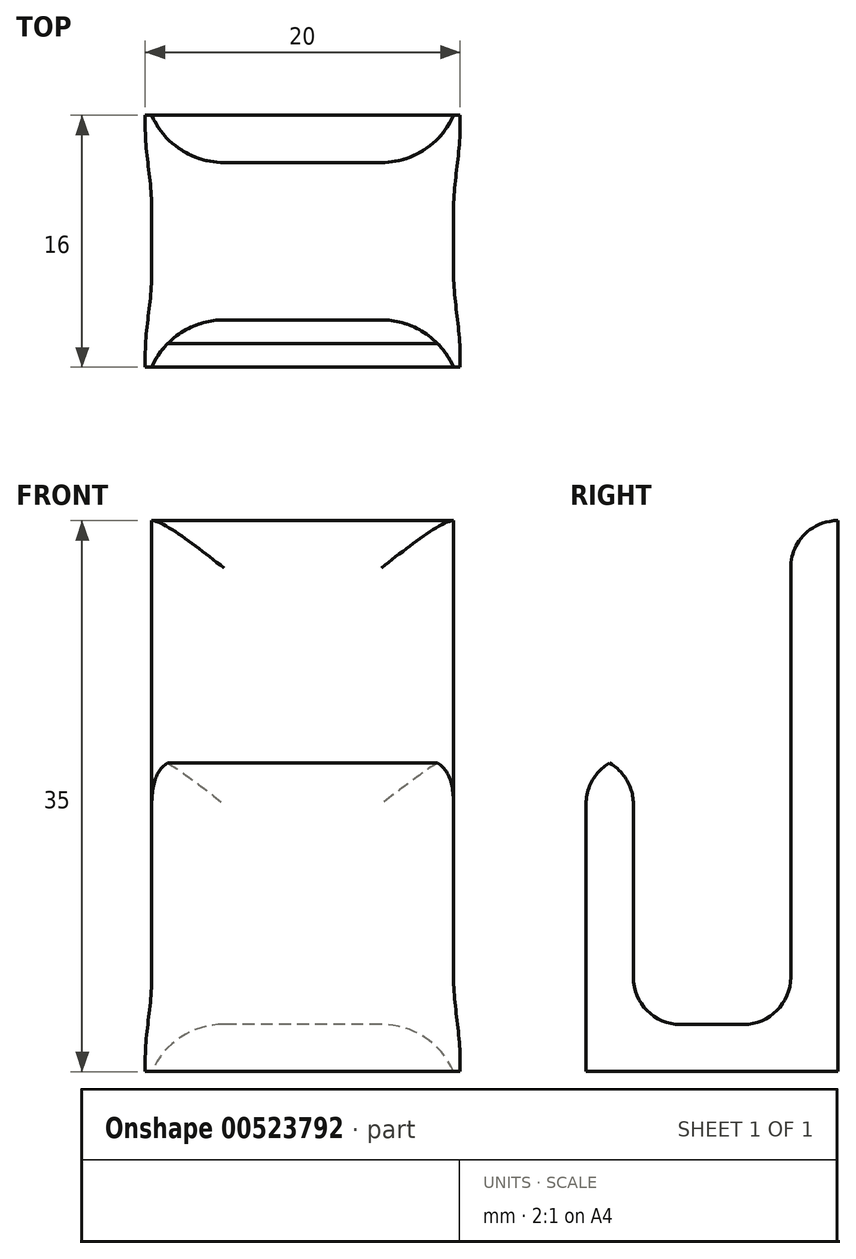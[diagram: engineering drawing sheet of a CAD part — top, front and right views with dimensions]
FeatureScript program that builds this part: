
annotation { "Feature Type Name" : "Feature", "Feature Type Description" : "" }
export const myFeature = defineFeature(function(context is Context, id is Id, definition is map)
    precondition{}
    {
        {
            var Q0;
            Q0=qCreatedBy(makeId("Right.planeOp"),FACE);
            var sketch = newSketch(context, id + "F0", { "sketchPlane" : qUnion([Q0])});
            skLineSegment(sketch, "E0.bottom", {"start": v(0, 24.94) * mm, "end": v(-3, 24.94) * mm});
            skLineSegment(sketch, "E0.left", {"start": v(0, 24.94) * mm, "end": v(0, -10.06) * mm});
            skLineSegment(sketch, "E0.right", {"start": v(-3, 24.94) * mm, "end": v(-3, -7.06) * mm});
            skLineSegment(sketch, "E1.top", {"start": v(-3, -7.06) * mm, "end": v(-13, -7.06) * mm});
            skLineSegment(sketch, "E2.top", {"start": v(-13, 9.94) * mm, "end": v(-16, 9.94) * mm});
            skLineSegment(sketch, "E2.left", {"start": v(-13, -7.06) * mm, "end": v(-13, 9.94) * mm});
            skLineSegment(sketch, "E2.right", {"start": v(-16, -10.06) * mm, "end": v(-16, 9.94) * mm});
            skLineSegment(sketch, "E3", {"start": v(0, -10.06) * mm, "end": v(-16, -10.06) * mm});
            skSolve(sketch);
        }
        {
            var Q0;
            Q0=makeQuery(id+"F0.imprint","IMPRINT",FACE,{"disambiguationData":[TD([[makeQuery(id+"F0.imprint","IMPRINT",EDGE,{"derivedFrom":sQuery(id+"F0.wireOp",EDGE,"E0.bottom")}),1.0]])]});
            extrude(context, id + "F1", {"entities" : qUnion([Q0]), "depth" : 20 * mm, "offsetDistance" : 25 * mm});
        }
        {
            var Q0;
            Q0=makeQuery(id+"F1.opExtrude","SWEPT_EDGE",EDGE,{"disambiguationData":[OSD([sQuery(id+"F0.wireOp",EDGE,"E0.bottom"),sQuery(id+"F0.wireOp",EDGE,"E0.right")])]});
            var Q1;
            Q1=makeQuery(id+"F1.opExtrude","SWEPT_EDGE",EDGE,{"disambiguationData":[OSD([sQuery(id+"F0.wireOp",EDGE,"E1.top"),sQuery(id+"F0.wireOp",EDGE,"E2.left")])]});
            var Q2;
            Q2=makeQuery(id+"F1.opExtrude","SWEPT_EDGE",EDGE,{"disambiguationData":[OSD([sQuery(id+"F0.wireOp",EDGE,"E2.top"),sQuery(id+"F0.wireOp",EDGE,"E2.left")])]});
            var Q3;
            Q3=makeQuery(id+"F1.opExtrude","SWEPT_EDGE",EDGE,{"disambiguationData":[OSD([sQuery(id+"F0.wireOp",EDGE,"E2.top"),sQuery(id+"F0.wireOp",EDGE,"E2.right")])]});
            var Q4;
            Q4=makeQuery(id+"F1.opExtrude","SWEPT_EDGE",EDGE,{"disambiguationData":[OSD([sQuery(id+"F0.wireOp",EDGE,"E0.right"),sQuery(id+"F0.wireOp",EDGE,"E1.top")])]});
            fillet(context, id + "F2", {"entities" : qUnion([Q0, Q1, Q2, Q3, Q4]), "radius" : 3 * mm, "tangentPropagation" : true, "allowEdgeOverflow" : false});
        }
        {
            var Q0;
            {var subQ0=sQuery(id+"F0.wireOp",EDGE,"E1.top");var subQ1=sQuery(id+"F0.wireOp",EDGE,"E0.right");Q0=makeQuery(id+"F2.opFillet","BLEND_EDGE",EDGE,{"blendedFrom":[makeQuery(id+"F1.opExtrude","SWEPT_EDGE",EDGE,{"disambiguationData":[OSD([subQ1,subQ0])]}),makeQuery(id+"F1.opExtrude","CAP_FACE",FACE,{"disambiguationData":[OSD([sQuery(id+"F0.wireOp",EDGE,"E0.bottom"),sQuery(id+"F0.wireOp",EDGE,"E0.left"),subQ1,subQ0,sQuery(id+"F0.wireOp",EDGE,"E2.top"),sQuery(id+"F0.wireOp",EDGE,"E2.left"),sQuery(id+"F0.wireOp",EDGE,"E2.right"),sQuery(id+"F0.wireOp",EDGE,"E3")])],"isStart":true})],"blendedInto":[makeQuery(id+"F1.opExtrude","CAP_FACE",FACE,{"disambiguationData":[OSD([sQuery(id+"F0.wireOp",EDGE,"E0.bottom"),sQuery(id+"F0.wireOp",EDGE,"E0.left"),subQ1,subQ0,sQuery(id+"F0.wireOp",EDGE,"E2.top"),sQuery(id+"F0.wireOp",EDGE,"E2.left"),sQuery(id+"F0.wireOp",EDGE,"E2.right"),sQuery(id+"F0.wireOp",EDGE,"E3")])],"isStart":true})]});}
            var Q1;
            {var subQ0=sQuery(id+"F0.wireOp",EDGE,"E1.top");var subQ1=sQuery(id+"F0.wireOp",EDGE,"E0.right");Q1=makeQuery(id+"F2.opFillet","BLEND_EDGE",EDGE,{"blendedFrom":[makeQuery(id+"F1.opExtrude","SWEPT_EDGE",EDGE,{"disambiguationData":[OSD([subQ1,subQ0])]}),makeQuery(id+"F1.opExtrude","CAP_FACE",FACE,{"disambiguationData":[OSD([sQuery(id+"F0.wireOp",EDGE,"E0.bottom"),sQuery(id+"F0.wireOp",EDGE,"E0.left"),subQ1,subQ0,sQuery(id+"F0.wireOp",EDGE,"E2.top"),sQuery(id+"F0.wireOp",EDGE,"E2.left"),sQuery(id+"F0.wireOp",EDGE,"E2.right"),sQuery(id+"F0.wireOp",EDGE,"E3")])],"isStart":false})],"blendedInto":[makeQuery(id+"F1.opExtrude","CAP_FACE",FACE,{"disambiguationData":[OSD([sQuery(id+"F0.wireOp",EDGE,"E0.bottom"),sQuery(id+"F0.wireOp",EDGE,"E0.left"),subQ1,subQ0,sQuery(id+"F0.wireOp",EDGE,"E2.top"),sQuery(id+"F0.wireOp",EDGE,"E2.left"),sQuery(id+"F0.wireOp",EDGE,"E2.right"),sQuery(id+"F0.wireOp",EDGE,"E3")])],"isStart":false})]});}
            fillet(context, id + "F3", {"entities" : qUnion([Q0, Q1]), "radius" : 5 * mm, "tangentPropagation" : true, "allowEdgeOverflow" : false});
        }
    });
